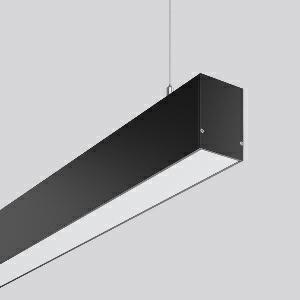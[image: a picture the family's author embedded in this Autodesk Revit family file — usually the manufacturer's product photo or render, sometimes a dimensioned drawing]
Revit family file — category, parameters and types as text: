
# Revit family: less_is_more_50_312311_003_1_99da
name_source: partatom
category: Lighting Fixtures
units: mm (PartAtom-declared; Revit-internal decimal feet)

## family parameters
Cut with Voids When Loaded = No
Host = Face
Light Source = No
Part Type = Normal
Room Calculation Point = No
Round Connector Dimension = Use Diameter
Shared = No

## types (1)
- LESS IS MORE 50 (1 x LED Modul 840, 2400 lm, 4000)
    Apparent Load = 22 VA
    CIE Flux Codes = 48 79 95 100 100
    Color Rendering = 80
    Color Temperature = 4000
    Default Elevation = 1800 mm
    Description = Series: LESS IS MORE 50
Linear pendant luminaire for aesthetically sophisticated lighting. Housing: extruded aluminium profile, powder-coated. End cap aluminium powder-coated. Canopy made of aluminium, powder-coated. Diffuser made of non-yellowing plastic (PMMA), opal. Direct light emission. Suitable for pendant. 2-point steel cable suspension freely positionable and infinitely height-adjustable. Special lengths available on request. LED unit with integrated converter interchangeable and removable. Suitable for through-wiring. With sensors or as a safety luminaire on request. 
Colour: deep black, matt (RAL 9005)
Length: 847 mm
Width: 57 mm
Height: 75 mm
Suspension length: 2000 mm
Lamp: LED
Socket: without socket
Colour temperature: 4000K
Colour rendering index (CRI): 80
System power: 22 W
Rated luminous flux: 2400 lm
Luminous efficiency: 109 lm/W
Control gear: Regulated power supply
Protection class: I
Type of protection: IP 20
    Height = 75 mm
    Lamp = 1 x LED Modul 840
    Lamp Light Flux = 2400 lm
    Lamp count = 1
    Length = 847 mm
    Lifetime = 50000 h
    Luminous efficacy = 109 lm/W
    Manufacturer = RZB
    ModVariant = No
    Model = 312311.003.1
    Mounting Place = Ceiling
    Mounting Type = Pendant
    Number of Poles = 1
    OnlyDefault = Yes
    Power Factor = 1
    Product Name = LESS IS MORE 50
    Product group = Pendant LED linear luminaires
    ProductGroupID = 907
    Protection Class = Protection class I
    Protection Degree = IP 20
    RLX_Detail_Level = 1
    RLX_Emergency_Light_Flux = 0 lm
    RLX_Emergency_Type = 0
    RLX_Emergency_Type_DB = No
    RlxData = <blob elided: 28881 chars, md5=aa848d99>
    Socket = socket
    Standby Power = 0 W
    System Light Flux = 2400 lm
    System Power = 22 W
    Type Comments = Product without accessories
    Type Image = 312318.003.jpg
    URL = http://relux.com
    VarID = ---
    Voltage = 230 V
    Voltage Range = 220-240 V
    Weight = 0.00 kg
    Width = 57 mm

## geometry (parser evidence)
native form markers: Blend x4, Sweep x9
no freeform markers — native parametric forms only
